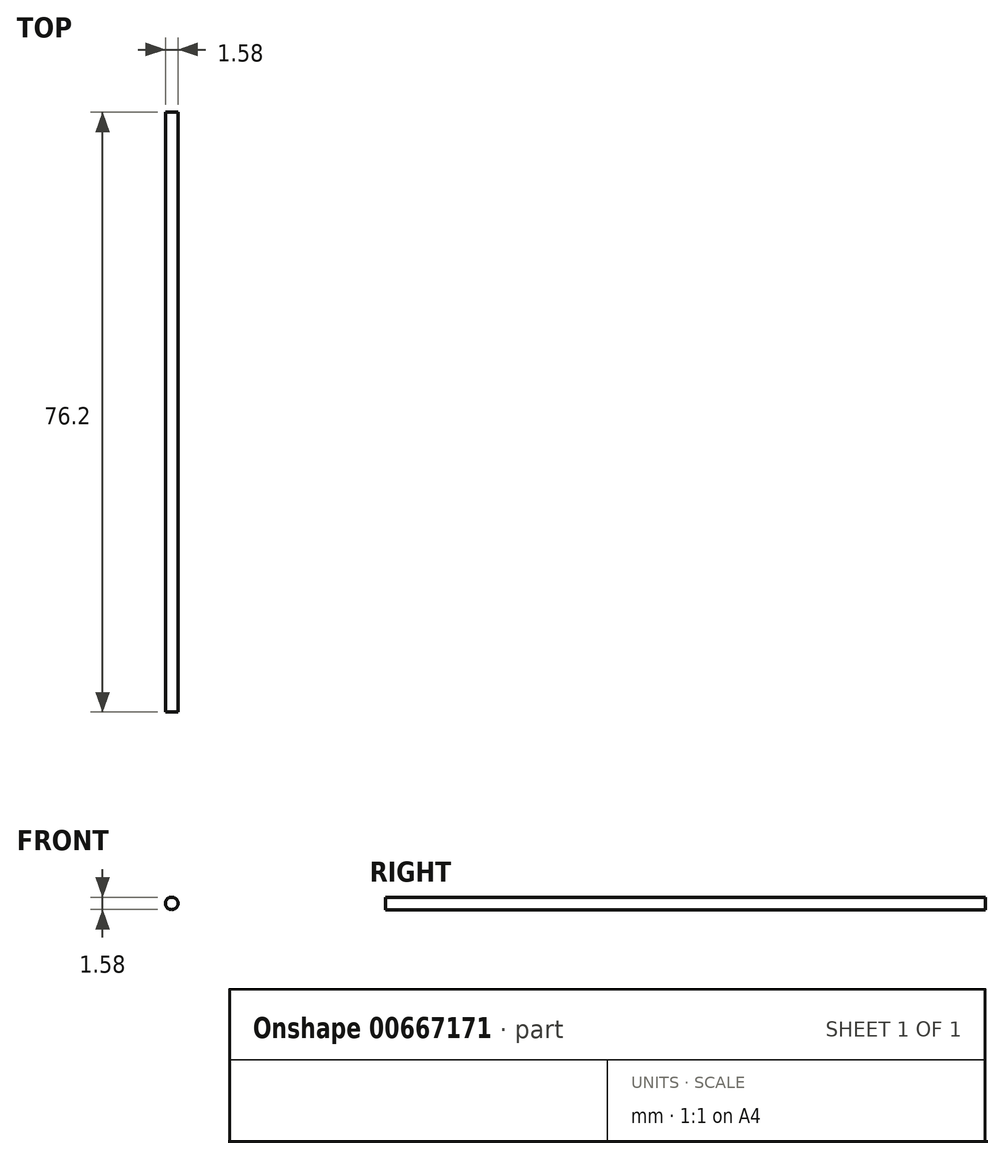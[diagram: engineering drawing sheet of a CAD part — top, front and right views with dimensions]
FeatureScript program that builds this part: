
annotation { "Feature Type Name" : "Feature", "Feature Type Description" : "" }
export const myFeature = defineFeature(function(context is Context, id is Id, definition is map)
    precondition{}
    {
        {
            var Q0;
            Q0=qCreatedBy(makeId("Front.planeOp"),FACE);
            var sketch = newSketch(context, id + "F0", { "sketchPlane" : qUnion([Q0])});
            skCircle(sketch, "E0", {"center": v(0, 0) * mm, "radius": 0.8 * mm});
            skSolve(sketch);
        }
        {
            var Q0;
            Q0 = qSketchRegion(id + "F0", true);
            extrude(context, id + "F1", {"entities" : qUnion([Q0]), "depth" : 76.2 * mm, "offsetDistance" : 25.4 * mm});
        }
        {
            var Q0;
            Q0 = qSketchRegion(id + "F0", true);
            extrude(context, id + "F2", {"entities" : qUnion([Q0]), "operationType" : NewBodyOperationType.ADD, "depth" : 25.4 * mm, "offsetDistance" : 25.4 * mm});
        }
    });
